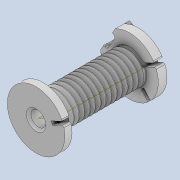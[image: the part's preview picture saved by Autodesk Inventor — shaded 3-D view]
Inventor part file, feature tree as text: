
AUTODESK INVENTOR PART (.ipt)
format: ipt  version: 2020 (Build 240168000, 168)  size: 1,081,344 bytes
history: native  units: mm
features: sketch x14, fillet x13, extrude x12, projected_geometry x12, other x4, thicken_offset x3, chamfer x2, plane x1, sweep x1, reference x1
ambient origin geometry x8: Origin, YZ Plane, XZ Plane, XY Plane, X Axis, Y Axis, Z Axis, Center Point
bodies: Solid1 (feature_tree)
feature tree (63):
  extrude  "Extrusion1"  Depth=12.0mm
  extrude  "Extrusion2"  Depth=3.0mm
  extrude  "Extrusion3"  Depth=18.0mm TaperAngle=0.0deg
  sketch  "3D Sketch1"
  plane  "Work Plane1"
  sweep  "Sweep1"
  extrude  "Extrusion4"  Depth=0.7mm
  extrude  "Extrusion5"  TaperAngle=0.0deg  [1 undecoded]
  fillet  "Fillet1"  Radius=5.0mm
  fillet  "Fillet2"  Radius=0.7mm
  fillet  "Fillet3"  Radius=1.0mm
  fillet  "Fillet4"  Radius=5.0mm
  fillet  "Fillet5"  Radius=0.7mm
  fillet  "Fillet6"  Radius=1.0mm
  extrude  "Extrusion6"  Depth=0.1mm
  thicken_offset  "Thicken1"
  thicken_offset  "Thicken2"
  extrude  "Extrusion7"  Depth=0.1mm
  extrude  "Extrusion8"  Depth=0.1mm
  extrude  "Extrusion9"  Depth=8.0mm
  chamfer  "Chamfer1"  Distance=2.0mm
  fillet  "Fillet7"  Radius=0.8mm
  fillet  "Fillet8"  Radius=0.8mm
  extrude  "Extrusion10"  Depth=0.5mm
  extrude  "Extrusion11"  Depth=0.4mm
  extrude  "Extrusion13"  Depth=0.4mm TaperAngle=0.0deg
  fillet  "Fillet10"  Radius=4.0mm
  fillet  "Fillet11"  Radius=0.8mm
  fillet  "Fillet12"  Radius=0.5mm
  fillet  "Fillet13"  Radius=0.5mm
  fillet  "Fillet14"  Radius=0.5mm
  thicken_offset  "Thicken3"
  chamfer  "Chamfer2"  Distance=3.490659mm
  sketch  "Sketch1"  dims[d0=3.0mm d1=12.0mm]
  reference  "Reference1"
  sketch  "Sketch2"  dims[d2=1.0mm d3=0.0mm d4=3.0mm]
  sketch  "Sketch3"  dims[d5=7.0mm d6=18.0mm d7=0.0mm]
  projected_geometry  "Projected Loop1"
  other  "Helical Curve2"
  sketch  "Sketch4"  dims[d8=1.0mm d9=0.0mm d14=18.0mm d15=160.0mm d16=7.0mm d17=0.0mm]
  projected_geometry  "Projected Loop2"
  projected_geometry  "Projected Loop3"
  sketch  "Sketch5"  dims[d18=0.5mm d19=0.7mm]
  projected_geometry  "Projected Loop4"
  sketch  "Sketch6"  dims[d20=0.5mm d21=0.0mm d22=0.0mm d23=5.0mm d24=0.7mm d25=1.0mm d26=0.0mm d27=5.0mm d28=0.7mm d29=1.0mm d30=0.0mm]
  projected_geometry  "Projected Loop5"
  sketch  "Sketch7"  dims[d31=1.0mm d32=0.1mm]
  projected_geometry  "Projected Loop6"
  sketch  "Sketch8"  dims[d33=0.1mm d34=0.1mm]
  projected_geometry  "Projected Loop7"
  sketch  "Sketch9"  dims[d35=1.0mm d36=0.1mm]
  projected_geometry  "Projected Loop8"
  sketch  "Sketch10"  dims[d37=30.0deg d38=8.0mm]
  projected_geometry  "Projected Loop9"
  sketch  "Sketch11"  dims[d39=6.0mm d40=2.0mm d41=0.0mm d42=0.8mm d43=0.8mm]
  projected_geometry  "Projected Loop10"
  sketch  "Sketch12"  dims[d44=0.5mm d45=0.5mm]
  projected_geometry  "Projected Loop11"
  sketch  "Sketch14"  dims[d46=4.0mm d47=0.0mm d48=1.4mm d49=4.0mm d50=0.0mm d51=4.0mm d52=0.8mm d53=0.0mm d54=0.5mm d55=2.0mm d56=45.0deg d57=0.5mm d58=0.5mm d59=3.490659mm d60=2.2mm d61=0.7mm d62=2.0mm d63=0.0mm d64=5.0mm d65=1.6mm d66=2.0mm d67=0.0mm d72=0.8mm d73=3.0mm d74=5.0mm d75=2.0mm d76=0.0mm d77=1.0mm d78=0.3mm d79=0.1mm d80=0.3mm d81=0.4mm d82=0.05mm d83=0.05mm d84=0.5mm d85=2.0mm d86=45.0deg]
  projected_geometry  "Projected Loop13"
  parser-record x1  (decoder bookkeeping rows leaked as tree rows — omitted from the tree; the rows remain in map.json)
  other  "tip2_ass_t1.iam"
  other  "bearing_3_6_2:1"
note: 1 required parameter value undecoded (feature->parameter linkage not recoverable at this tier; creation-order binding heuristic only, values carry confidence <= 0.55)
note: 1 file-system path scrubbed to <path> (originals preserved in map.json)
